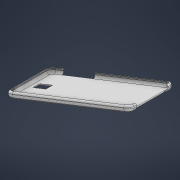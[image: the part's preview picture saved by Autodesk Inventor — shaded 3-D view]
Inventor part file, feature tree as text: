
AUTODESK INVENTOR PART (.ipt)
format: ipt  version: 2021 (Build 250183000, 183)  size: 4,001,792 bytes
history: native  units: mm
features: other x10, extrude x7, sketch x6, fillet x5, chamfer x4, thicken_offset x2, plane x2, surface_op x1
ambient origin geometry x8: Origin, YZ Plane, XZ Plane, XY Plane, X Axis, Y Axis, Z Axis, Center Point
bodies: Solid1 (feature_tree), Solid2 (feature_tree), Solid5 (feature_tree)
feature tree (37):
  other  "Blocks"
  extrude  "Extrusion1"  Depth=137.5mm
  fillet  "Fillet1"  [1 undecoded]
  fillet  "Fillet2"  Radius=9.9mm
  fillet  "Fillet3"  Radius=1.46mm
  thicken_offset  "Thicken1"
  chamfer  "Chamfer2"  [1 undecoded]
  extrude  "Extrusion2"  Depth=6.0mm TaperAngle=0.0deg
  plane  "Work Plane1"
  plane  "Work Plane2"
  other  "Ruled Surface6"
  surface_op  "Sculpt1"
  extrude  "Extrusion3"  Depth=6.0mm TaperAngle=0.0deg
  extrude  "Extrusion5"  Depth=2.0mm
  fillet  "Fillet5"  Radius=8.0mm
  thicken_offset  "Thicken2"
  chamfer  "Chamfer3"  Distance=8.0mm
  extrude  "Extrusion11"  Depth=8.0mm
  fillet  "Fillet6"  Radius=8.0mm
  chamfer  "Chamfer4"  Distance=5.9mm
  sketch  "Sketch17"  dims[d31=5.9mm d32=2.0mm]
  extrude  "Extrusion9"  Depth=24.5mm
  extrude  "Extrusion10"  Depth=19.0mm
  chamfer  "Chamfer5"  Distance=19.0mm
  sketch  "Sketch1"  dims[d0=208.4mm d1=137.5mm d3=0.0mm d4=9.9mm d7=1.46mm d8=0.8mm d18=0.0mm d19=0.0mm]
  sketch  "Sketch3"  dims[d20=53.5mm d22=6.0mm d23=0.0mm]
  sketch  "Sketch4"  dims[d28=5.9mm d29=6.0mm d30=0.0mm]
  other  "Srf7"
  other  "Ruled Surface7"
  other  "Srf8"
  sketch  "3D Sketch9"
  other  "Ruled Surface8"
  other  "Srf9"
  other  "pika"
  sketch  "Sketch18"  dims[d33=2.0mm d34=3.5mm d35=10.0mm d36=3.5mm d37=10.0mm d38=5.0mm d39=0.0mm d40=5.0mm d41=10.0mm d42=8.0mm d43=8.0mm d44=8.0mm d45=8.0mm d46=5.9mm d47=24.5mm d48=19.0mm d49=19.0mm d53=0.5mm d54=2.0mm d55=45.0deg d87=10.0mm d88=5.585054mm d89=10.0mm d90=0.0mm d91=10.0mm d92=45.0deg d108=2.0mm d109=1.0mm d110=1.0mm d111=1.0mm d112=2.0mm d113=45.0deg d116=0.4mm d117=0.0mm d118=0.4mm d119=0.0mm d120=22.0mm d121=8.0mm d122=52.75mm d123=52.75mm d124=0.0mm d125=0.0mm d126=1.0mm d127=1.5mm d128=2.46mm d129=45.0deg d130=0.2mm d131=2.0mm d132=45.0deg]
  other  "3D Intersection3"
  other  "pika:1"
note: 2 required parameter values undecoded (feature->parameter linkage not recoverable at this tier; creation-order binding heuristic only, values carry confidence <= 0.55)
